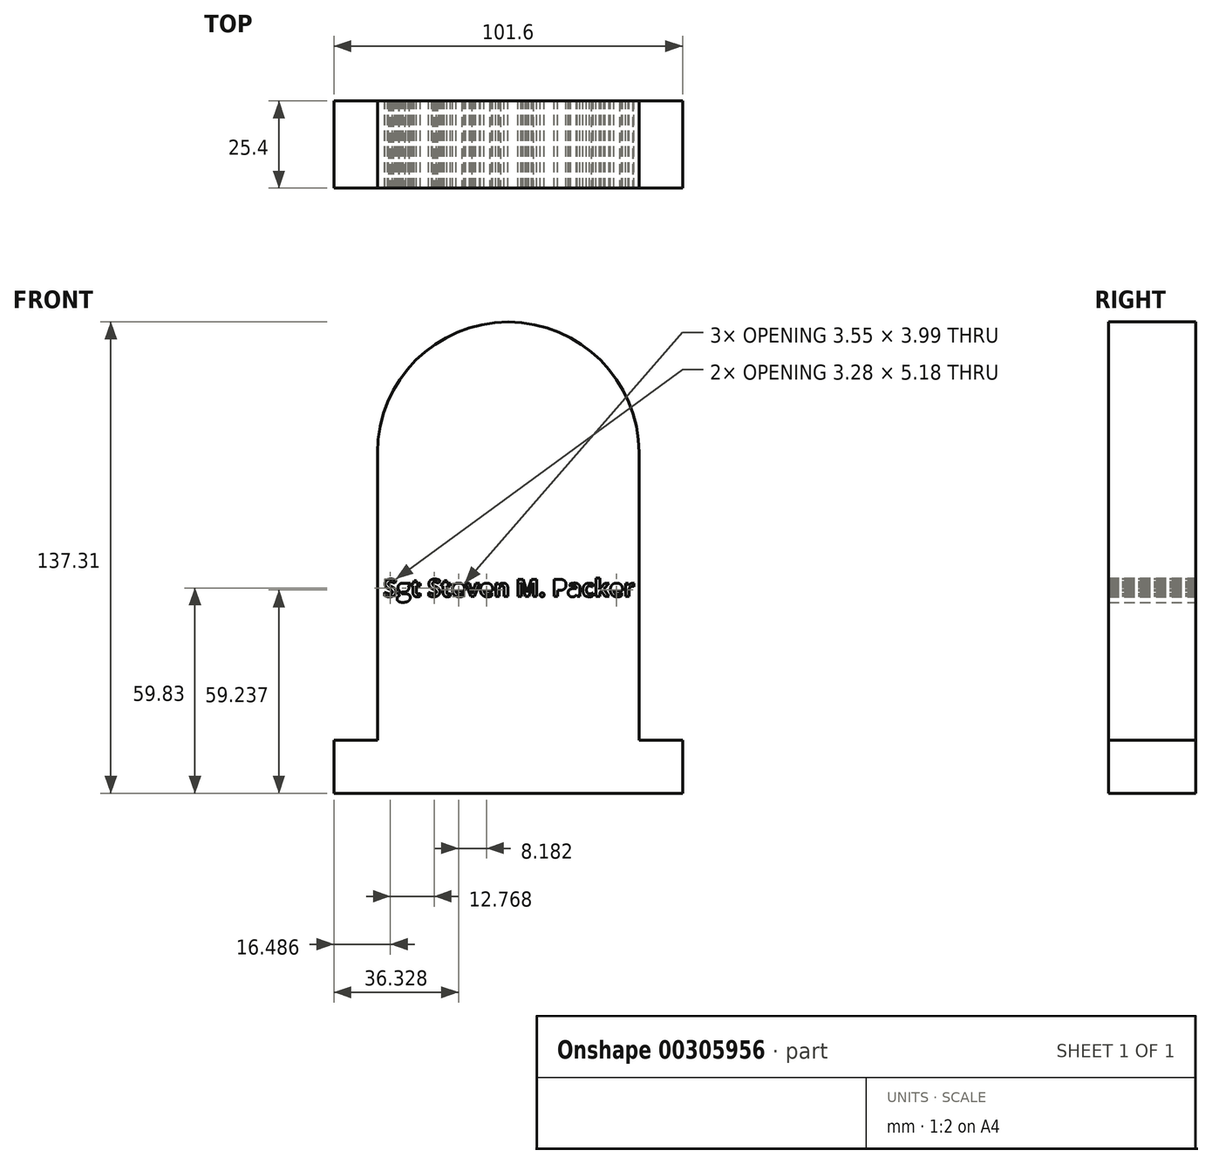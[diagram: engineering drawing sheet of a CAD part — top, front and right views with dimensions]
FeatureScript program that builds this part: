
annotation { "Feature Type Name" : "Feature", "Feature Type Description" : "" }
export const myFeature = defineFeature(function(context is Context, id is Id, definition is map)
    precondition{}
    {
        {
            var Q0;
            Q0=qCreatedBy(makeId("Front.planeOp"),FACE);
            var sketch = newSketch(context, id + "F0", { "sketchPlane" : qUnion([Q0])});
            skLineSegment(sketch, "E0.bottom", {"start": v(-36.09, 7.27) * mm, "end": v(40.11, 7.27) * mm});
            skLineSegment(sketch, "E0.top", {"start": v(-36.09, -76.54) * mm, "end": v(40.11, -76.54) * mm});
            skLineSegment(sketch, "E0.left", {"start": v(-36.09, 7.27) * mm, "end": v(-36.09, -76.54) * mm});
            skLineSegment(sketch, "E0.right", {"start": v(40.11, 7.27) * mm, "end": v(40.11, -76.54) * mm});
            skArc(sketch, "E1", {"start": v(40.11, 7.27) * mm, "mid": v(2.01, 45.37) * mm, "end": v(-36.09, 7.27) * mm});
            skLineSegment(sketch, "E2", {"start": v(40.11, -76.54) * mm, "end": v(52.81, -76.54) * mm});
            skLineSegment(sketch, "E3", {"start": v(-36.09, -76.54) * mm, "end": v(-48.79, -76.54) * mm});
            skLineSegment(sketch, "E4", {"start": v(52.81, -76.54) * mm, "end": v(52.81, -91.94) * mm});
            skLineSegment(sketch, "E5", {"start": v(52.81, -91.94) * mm, "end": v(-48.79, -91.94) * mm});
            skLineSegment(sketch, "E6", {"start": v(-48.79, -91.94) * mm, "end": v(-48.79, -76.54) * mm});
            skText(sketch, "E7", { "text": "Sgt Steven M. Packer\n", "fontName": "OpenSans-Bold.ttf"});
            skPoint(sketch, "E7.secondSnap0", {"position": v(40.11, -34.63) * mm});
            const initialGuessF0  = {"E7": [-0.03427, -0.03463, 1, 0, 0.00508]};
            skSetInitialGuess(sketch, initialGuessF0);
            skSolve(sketch);
        }
        {
            var Q0;
            Q0=makeQuery(id+"F0.imprint","IMPRINT",FACE,{"disambiguationData":[TD([[makeQuery(id+"F0.imprint","IMPRINT",EDGE,{"derivedFrom":sQuery(id+"F0.wireOp",EDGE,"E0.bottom")}),1.0]])]});
            var Q1;
            Q1=makeQuery(id+"F0.imprint","IMPRINT",FACE,{"disambiguationData":[TD([[makeQuery(id+"F0.imprint","IMPRINT",EDGE,{"derivedFrom":sQuery(id+"F0.wireOp",EDGE,"E0.bottom")}),-1.0]])]});
            extrude(context, id + "F1", {"entities" : qUnion([Q0, Q1]), "depth" : 25.4 * mm});
        }
        {
            var Q0;
            Q0 = qSketchRegion(id + "F0", true);
            extrude(context, id + "F2", {"entities" : qUnion([Q0]), "operationType" : NewBodyOperationType.ADD, "depth" : 25.4 * mm});
        }
    });
